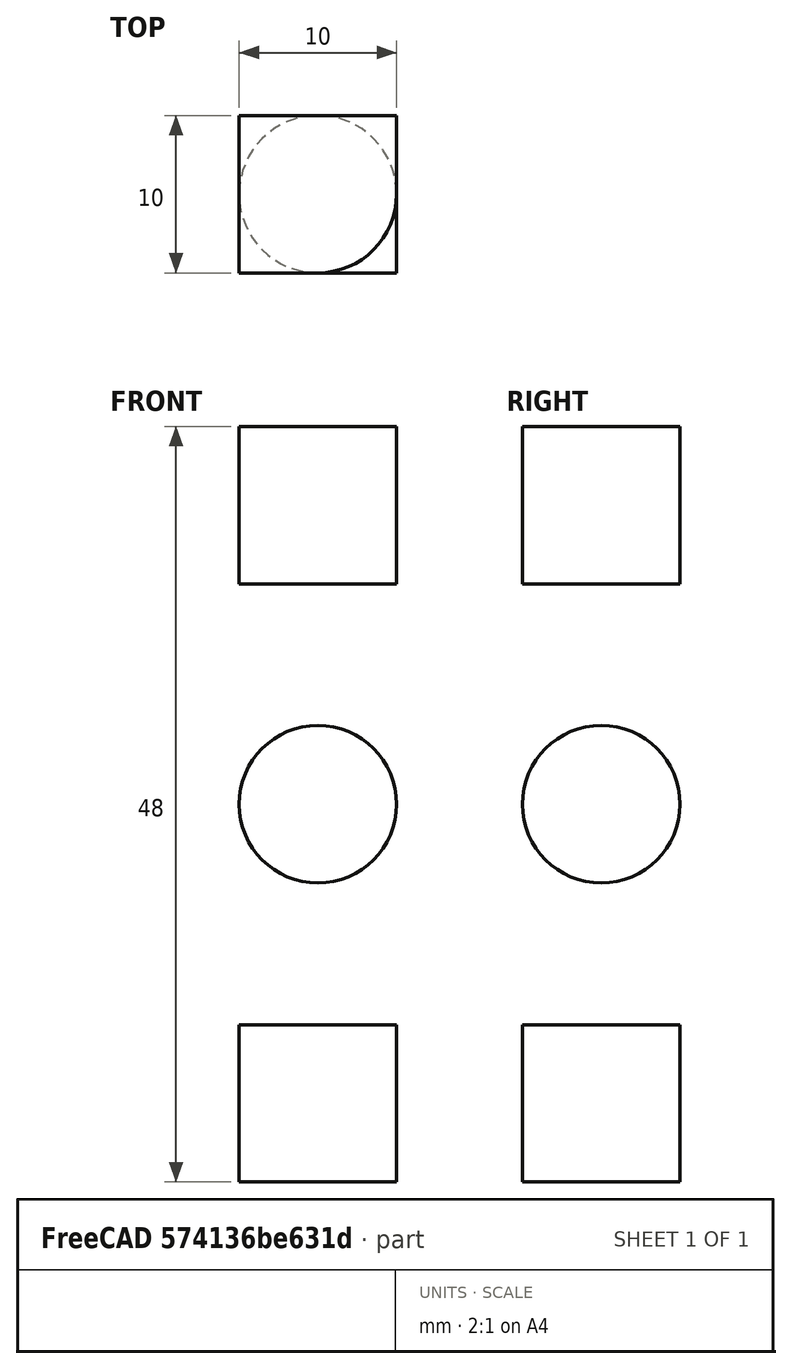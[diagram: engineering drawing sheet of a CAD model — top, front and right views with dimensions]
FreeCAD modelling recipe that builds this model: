
FCSTD DOCUMENT  (FreeCAD 1.1R44874 (Git))
Label: main
License: All rights reserved
LicenseURL: https://en.wikipedia.org/wiki/All_rights_reserved
objects: App::LinkGroupPython×3, Part::Box×2, Part::FeaturePython×2, Part::Sphere×1
note: 5 computed .brp shape members not serialized (recipe doc carries the construction recipe); baked Part::Feature solids carry a one-line shape summary decoded from their .brp

FEATURE [Part::Sphere] Sphere
  Angle1 = -90
  Angle2 = 90
  Angle3 = 360
  AttacherType = Attacher::AttachEngine3D
  Placement = pos=(0,0,24) rot=(0,0,1;0rad)
  Radius = 5
FEATURE [Part::Box] Box  label="Cube"
  AttacherType = Attacher::AttachEngine3D
  Height = 10
  Length = 10
  Placement = pos=(-5,-5,0) rot=(0,0,1;0rad)
  Width = 10
FEATURE [Part::Box] Box001  label="Cube001"
  AttacherType = Attacher::AttachEngine3D
  Height = 10
  Length = 10
  Placement = pos=(-5,-5,38) rot=(0,0,1;0rad)
  Width = 10
FEATURE [App::LinkGroupPython] OpticalLensGroup  label="OpticalLensGroup001"  # WARN: FeaturePython — macro-defined, semantics opaque (R4)
  AbsorptionLength = inf
  ElementList = -> [Sphere]
  GratingDiffractionOrder = 1
  GratingLinesOrientation = (0,0,1)
  GratingLinesPerMillimeter = 1000
  GratingType = 0
  LinkMode = 0
  ModifyPhiDomain = 0, 2*pi
  ModifyThetaDomain = -pi/2, pi/2
  OpticalType = 1
  PowerPhiDomain = 0, 2*pi
  PowerThetaDomain = -pi/2, pi/2
  RecordHits = false
  Reflectivity = 1
  RefractiveIndex = 1.15
FEATURE [App::LinkGroupPython] OpticalSurfaceSource  # WARN: FeaturePython — macro-defined, semantics opaque (R4)
  ActiveSurfaces = -> [Box001]
  FanModeRayCount = 100
  LinkMode = 0
  MaxIntersectionsScale = 1
  MaxRayLengthScale = 1
  PowerDensity = exp(-100*theta**2)
  RadiusResolutionNumericMode = 100000
  RandomNumberGeneratorMode = ?
  RaysPerIterationScale = 1
  RecordRays = false
  ThetaDomain = 0, 1e-6
  ThetaResolutionNumericMode = 100000
  UVSamplingInitialResolution = 5
  UVSamplingMaxRelAreaElementChange = 0.1
  Wavelength = 500
FEATURE [App::LinkGroupPython] OpticalAbsorberGroup  label="OpticalAbsorberGroup001"  # WARN: FeaturePython — macro-defined, semantics opaque (R4)
  AbsorptionLength = inf
  ElementList = -> [Box]
  GratingDiffractionOrder = 1
  GratingLinesOrientation = (0,0,1)
  GratingLinesPerMillimeter = 1000
  GratingType = 0
  LinkMode = 0
  ModifyPhiDomain = 0, 2*pi
  ModifyThetaDomain = -pi/2, pi/2
  OpticalType = 3
  PowerPhiDomain = 0, 2*pi
  PowerThetaDomain = -pi/2, pi/2
  RecordHits = true
  Reflectivity = 1
  RefractiveIndex = 2
FEATURE [Part::FeaturePython] OpticalSimulationSettings  label="cfg"  # WARN: FeaturePython — macro-defined, semantics opaque (R4)
  Active = false
  DistanceTolerance = 1e-06
  EnableStoreSingleShotData = false
  EndAfterHits = inf
  EndAfterIterations = inf
  EndAfterRays = inf
  MaxIntersections = 100
  MaxRayLength = 1000
  RaysPerIteration = 100
  SequentialMode = false
  ShowRaysInContinuousMode = true
  StoreHitFanIndex = false
  StoreHitInitDirection = false
  StoreHitInitPhi = false
  StoreHitInitPoint = false
  StoreHitInitPower = false
  StoreHitInitTheta = false
  StoreHitInitWavelength = false
  StoreHitRayIndex = false
  StoreHitTotalFanCount = false
  StoreHitTotalRaysInFan = false
  WorkerProcessCount = num_cpus
FEATURE [Part::FeaturePython] OpticalSimulationSettings001  label="sequentialCfg"  # WARN: FeaturePython — macro-defined, semantics opaque (R4)
  Active = true
  DistanceTolerance = 1e-06
  EnableStoreSingleShotData = false
  EndAfterHits = inf
  EndAfterIterations = inf
  EndAfterRays = inf
  MaxIntersections = 100
  MaxRayLength = 1000
  RaysPerIteration = 100
  SequentialMode = true
  SequentialModeElements_00 = -> [OpticalLensGroup]
  SequentialModeElements_01 = -> [OpticalAbsorberGroup]
  ShowRaysInContinuousMode = true
  StoreHitFanIndex = false
  StoreHitInitDirection = false
  StoreHitInitPhi = false
  StoreHitInitPoint = false
  StoreHitInitPower = false
  StoreHitInitTheta = false
  StoreHitInitWavelength = false
  StoreHitRayIndex = false
  StoreHitTotalFanCount = false
  StoreHitTotalRaysInFan = false
  WorkerProcessCount = num_cpus
